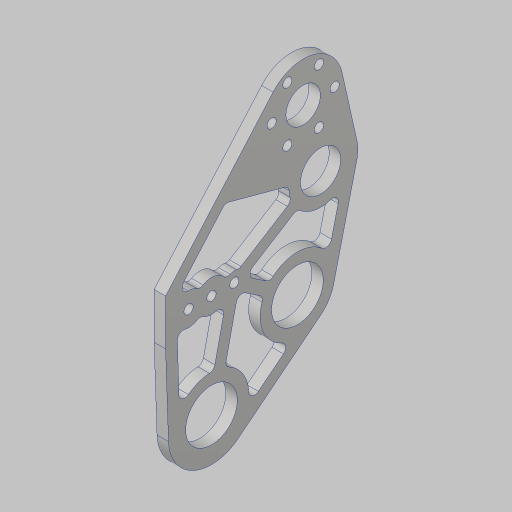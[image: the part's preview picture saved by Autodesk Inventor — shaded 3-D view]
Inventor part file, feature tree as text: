
AUTODESK INVENTOR PART (.ipt)
format: ipt  version: 2023.5 (Build 275446000, 446)  size: 287,744 bytes
history: native  units: in
note: dims shown in document units (in); Inventor stores cm internally (conversion verified against a paired STEP export)
features: sketch x2, extrude x2, hole x1, fillet x1, projected_geometry x1
ambient origin geometry x8: Origin, YZ Plane, XZ Plane, XY Plane, X Axis, Y Axis, Z Axis, Center Point
bodies: Solid1 (feature_tree)
feature tree (7):
  sketch  "Sketch1"  dims[d0=1.0in d1=2.0in]
  extrude  "Extrusion1"  Depth=2.0in
  hole  "Hole1"  [1 undecoded]
  extrude  "Extrusion2"  Depth=0.13in
  fillet  "Fillet1"  Radius=5.0in
  sketch  "Sketch2"  dims[d2=1.125in d3=2.25in d4=3.0in d5=5.0in d6=1.949in d11=0.5in d12=0.5in d13=0.375in d18=0.4688in d19=2.5in d20=1.375in d21=1.74in d22=8.0in d23=1.0in d24=2.1066in d25=0.25in d26=0.0in d27=0.75in d29=2.3622in d31=360.0deg d33=0.201in d34=0.75in d35=0.385in d36=0.25in d37=0.5635in d38=1.0in d39=0.8108in d40=1.0in d41=3.3in d42=1.6in d43=3.0in d44=1.4348in d46=0.25in d48=0.5in d49=1.0in d50=0.875in d51=0.875in d52=0.25in d53=0.25in d54=0.25in d55=0.125in d56=0.25in d57=0.125in d58=0.125in d59=0.125in d60=0.125in d61=0.125in d62=0.25in d63=1.0in d64=0.0in d65=0.13in]
  projected_geometry  "Project Cut Edges1"
note: 1 required parameter value undecoded (feature->parameter linkage not recoverable at this tier; creation-order binding heuristic only, values carry confidence <= 0.55)
